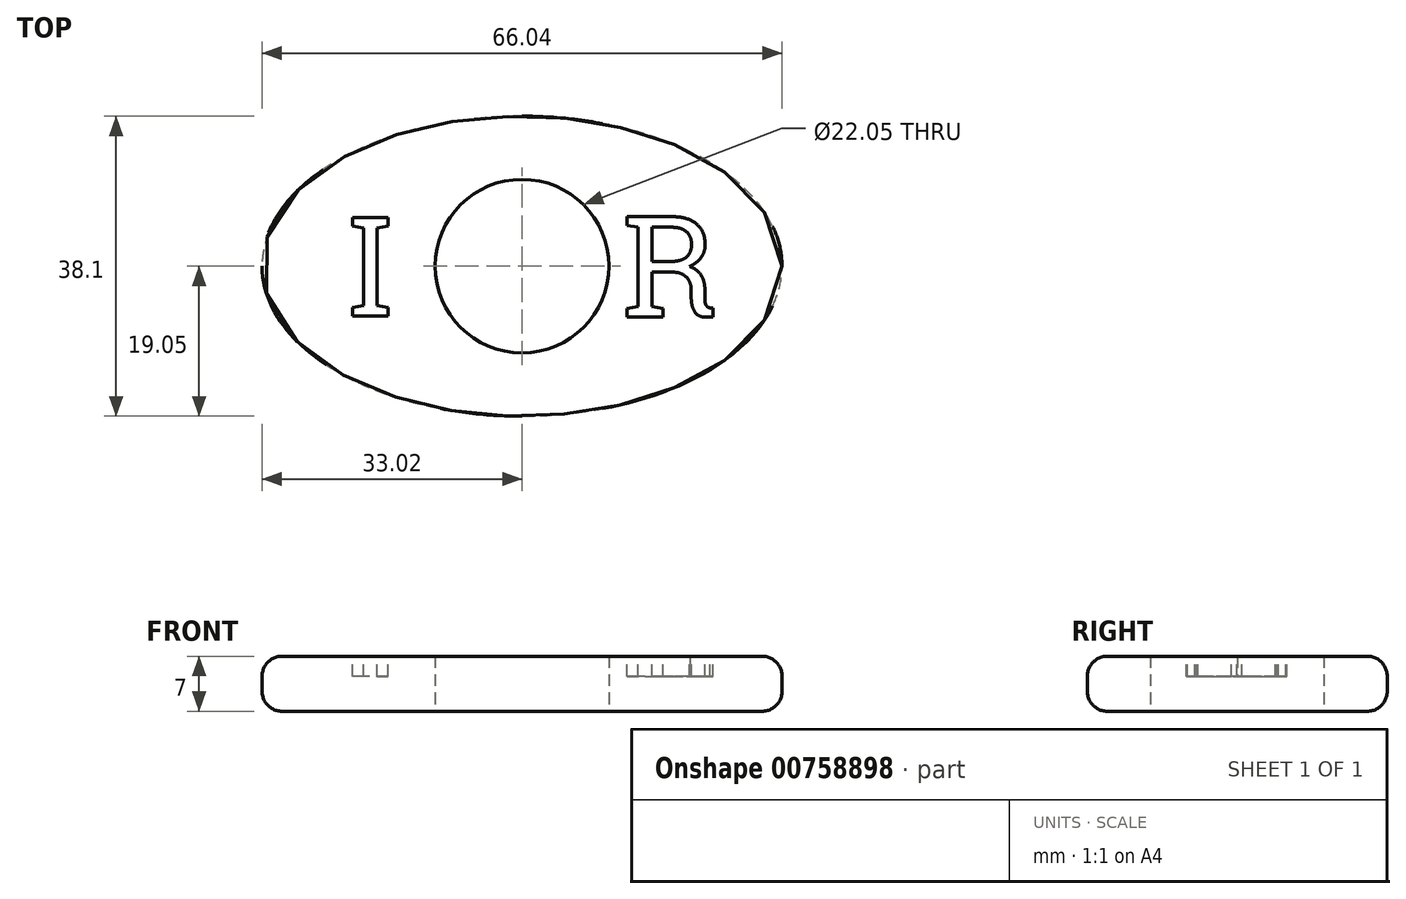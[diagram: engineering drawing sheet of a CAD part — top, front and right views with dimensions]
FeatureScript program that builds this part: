
annotation { "Feature Type Name" : "Feature", "Feature Type Description" : "" }
export const myFeature = defineFeature(function(context is Context, id is Id, definition is map)
    precondition{}
    {
        {
            var Q0;
            Q0=qCreatedBy(makeId("Top.planeOp"),FACE);
            var sketch = newSketch(context, id + "F0", { "sketchPlane" : qUnion([Q0])});
            skEllipse(sketch, "E0", {"center": v(0, 0) * mm, "majorRadius": 33.02 * mm, "minorRadius": 19.05 * mm, "majorAxis": v(1, 0)});
            skCircle(sketch, "E1", {"center": v(0, 0) * mm, "radius": 11.03 * mm});
            skLineSegment(sketch, "E2", {"start": v(-33.02, 0) * mm, "end": v(33.02, 0) * mm, "construction": true});
            skLineSegment(sketch, "E3", {"start": v(0, 19.05) * mm, "end": v(0, -19.05) * mm, "construction": true});
            skSolve(sketch);
        }
        {
            var Q0;
            Q0=makeQuery(id+"F0.imprint","IMPRINT",FACE,{"disambiguationData":[TD([[makeQuery(id+"F0.imprint","IMPRINT",EDGE,{"derivedFrom":sQuery(id+"F0.wireOp",EDGE,"E0")}),1.0]])]});
            extrude(context, id + "F1", {"entities" : qUnion([Q0]), "depth" : 7 * mm, "offsetDistance" : 25.4 * mm});
        }
        {
            var Q0;
            Q0=makeQuery(id+"F1.opExtrude","CAP_EDGE",EDGE,{"disambiguationData":[OSD([sQuery(id+"F0.wireOp",EDGE,"E0")])],"isStart":false});
            var Q1;
            Q1=makeQuery(id+"F1.opExtrude","CAP_EDGE",EDGE,{"disambiguationData":[OSD([sQuery(id+"F0.wireOp",EDGE,"E0")])],"isStart":true});
            fillet(context, id + "F2", {"entities" : qUnion([Q0, Q1]), "radius" : 2.54 * mm, "tangentPropagation" : true, "allowEdgeOverflow" : false});
        }
        {
            var Q0;
            Q0=makeQuery(id+"F1.opExtrude","CAP_FACE",FACE,{"disambiguationData":[OSD([sQuery(id+"F0.wireOp",EDGE,"E0"),sQuery(id+"F0.wireOp",EDGE,"E1")])],"isStart":false});
            var sketch = newSketch(context, id + "F3", { "sketchPlane" : qUnion([Q0])});
            skSolve(sketch);
        }
        {
            var Q0;
            {var subQ0=sQuery(id+"F0.wireOp",EDGE,"E1");Q0=makeQuery(id+"F3.imprint","IMPRINT",FACE,{"disambiguationData":[TD([[makeQuery(id+"F3.imprint","IMPRINT",EDGE,{"derivedFrom":makeQuery(id+"F1.opExtrude","CAP_EDGE",EDGE,{"disambiguationData":[OSD([subQ0])],"isStart":false})}),-1.0]])]});}
            var sketch = newSketch(context, id + "F4", { "sketchPlane" : qUnion([Q0])});
            skText(sketch, "E4", { "text": "I", "fontName": "RobotoSlab-Regular.ttf"});
            skText(sketch, "E5", { "text": "R", "fontName": "RobotoSlab-Regular.ttf"});
            skLineSegment(sketch, "E6", {"start": v(0, 0) * mm, "end": v(-25.4, 0) * mm, "construction": true});
            skLineSegment(sketch, "E7", {"start": v(0, 0) * mm, "end": v(25.4, 0) * mm, "construction": true});
            skLineSegment(sketch, "E8", {"start": v(-25.4, 0) * mm, "end": v(-12.7, 0) * mm, "construction": true});
            skLineSegment(sketch, "E9", {"start": v(12.7, 0) * mm, "end": v(25.4, 0) * mm});
            skPoint(sketch, "E10", {"position": v(19.05, 0) * mm});
            skLineSegment(sketch, "E11", {"start": v(12.7, 0) * mm, "end": v(25.4, 0) * mm, "construction": true});
            skPoint(sketch, "E12", {"position": v(-19.05, 0) * mm});
            const initialGuessF4  = {"E4": [-0.02215, -0.00635, 1, 0, 0.0127], "E5": [0.0127, -0.00648, 1, 0, 0.01295]};
            skSetInitialGuess(sketch, initialGuessF4);
            skSolve(sketch);
        }
        {
            var Q0;
            Q0=qSketchRegion(id+"F4",true);
            extrude(context, id + "F5", {"entities" : qUnion([Q0]), "operationType" : NewBodyOperationType.REMOVE, "oppositeDirection" : true, "depth" : 2.54 * mm, "offsetDistance" : 25.4 * mm});
        }
    });
